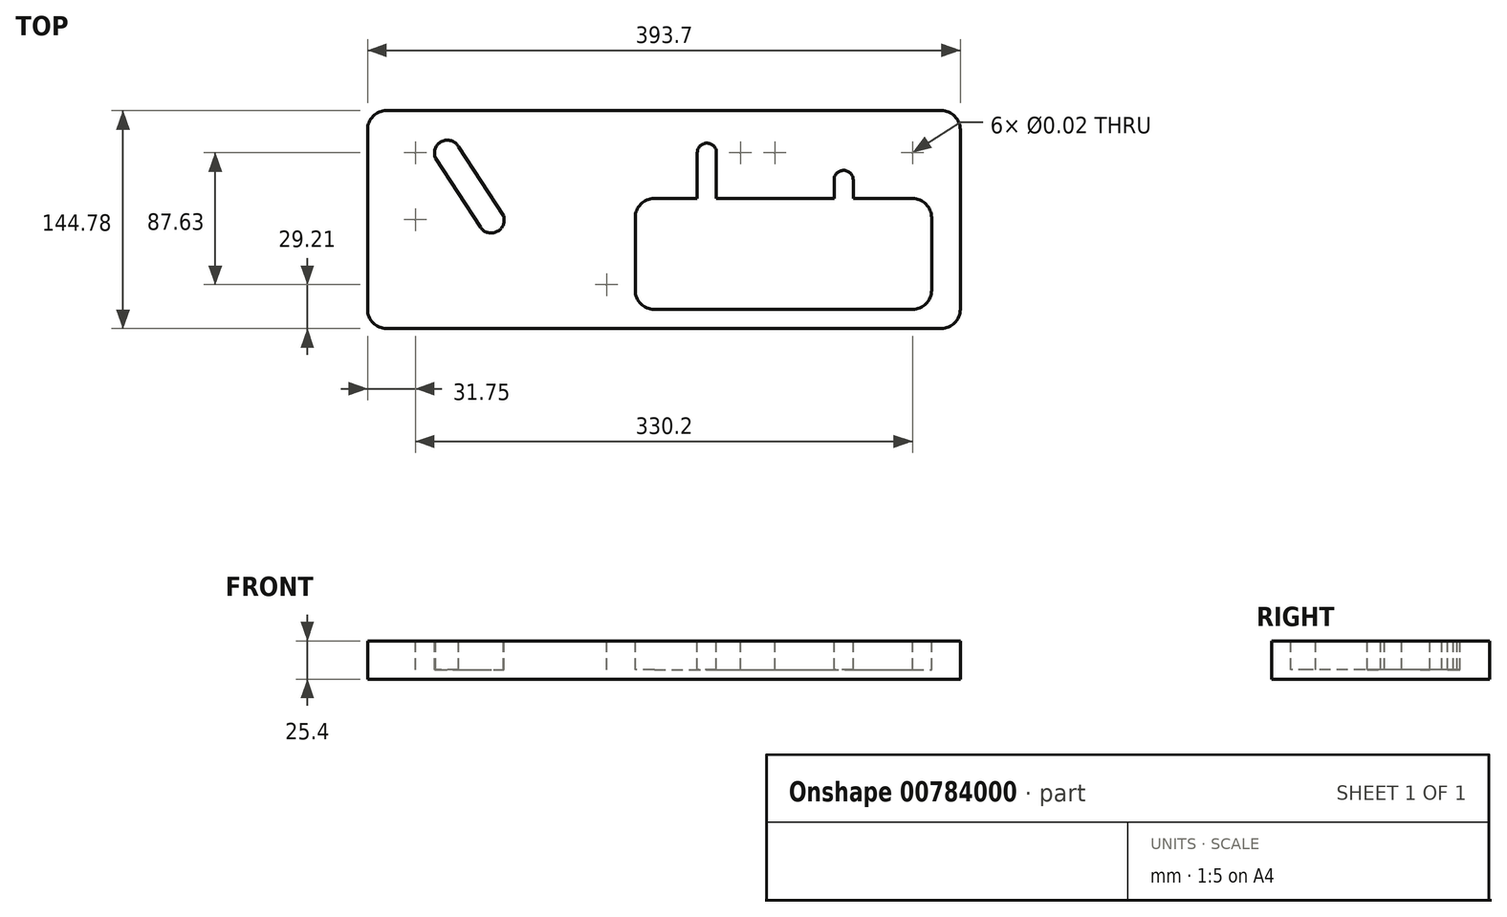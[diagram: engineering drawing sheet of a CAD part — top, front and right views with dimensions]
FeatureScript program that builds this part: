
annotation { "Feature Type Name" : "Feature", "Feature Type Description" : "" }
export const myFeature = defineFeature(function(context is Context, id is Id, definition is map)
    precondition{}
    {
        {
            var Q0;
            Q0=qCreatedBy(makeId("Top.planeOp"),FACE);
            var sketch = newSketch(context, id + "F0", { "sketchPlane" : qUnion([Q0])});
            skLineSegment(sketch, "E0.bottom", {"start": v(-184.15, -72.4) * mm, "end": v(184.15, -72.4) * mm});
            skLineSegment(sketch, "E0.top", {"start": v(-184.15, 72.4) * mm, "end": v(184.15, 72.4) * mm});
            skLineSegment(sketch, "E0.left", {"start": v(-196.85, -59.7) * mm, "end": v(-196.85, 59.7) * mm});
            skLineSegment(sketch, "E0.right", {"start": v(196.85, -59.7) * mm, "end": v(196.85, 59.7) * mm});
            skPoint(sketch, "E0.middle", {"position": v(0, 0) * mm});
            skPoint(sketch, "E1.visualSharp", {"position": v(-196.85, 72.4) * mm});
            skArc(sketch, "E1.filletArc", {"start": v(-184.15, 72.4) * mm, "mid": v(-193.13, 68.67) * mm, "end": v(-196.85, 59.7) * mm});
            skPoint(sketch, "E2.visualSharp", {"position": v(-196.85, -72.4) * mm});
            skArc(sketch, "E2.filletArc", {"start": v(-196.85, -59.7) * mm, "mid": v(-193.13, -68.67) * mm, "end": v(-184.15, -72.4) * mm});
            skPoint(sketch, "E3.visualSharp", {"position": v(196.85, 72.4) * mm});
            skArc(sketch, "E3.filletArc", {"start": v(196.85, 59.7) * mm, "mid": v(193.13, 68.67) * mm, "end": v(184.15, 72.4) * mm});
            skPoint(sketch, "E4.visualSharp", {"position": v(196.85, -72.4) * mm});
            skArc(sketch, "E4.filletArc", {"start": v(184.15, -72.4) * mm, "mid": v(193.13, -68.67) * mm, "end": v(196.85, -59.7) * mm});
            skSolve(sketch);
        }
        {
            var Q0;
            Q0 = qSketchRegion(id + "F0", true);
            extrude(context, id + "F1", {"entities" : qUnion([Q0]), "depth" : -25.4 * mm, "offsetDistance" : 25.4 * mm});
        }
        {
            var Q0;
            Q0=qCreatedBy(makeId("Top.planeOp"),FACE);
            var sketch = newSketch(context, id + "F2", { "sketchPlane" : qUnion([Q0])});
            skLineSegment(sketch, "E5.bottom", {"start": v(-6.35, 13.97) * mm, "end": v(165.1, 13.97) * mm});
            skLineSegment(sketch, "E5.top", {"start": v(-6.35, -59.7) * mm, "end": v(165.1, -59.7) * mm});
            skLineSegment(sketch, "E5.left", {"start": v(-19.05, 1.27) * mm, "end": v(-19.05, -47) * mm});
            skLineSegment(sketch, "E5.right", {"start": v(177.8, 1.27) * mm, "end": v(177.8, -47) * mm});
            skPoint(sketch, "E6.visualSharp", {"position": v(-19.05, 13.97) * mm});
            skArc(sketch, "E6.filletArc", {"start": v(-6.35, 13.97) * mm, "mid": v(-15.33, 10.25) * mm, "end": v(-19.05, 1.27) * mm});
            skPoint(sketch, "E7.visualSharp", {"position": v(177.8, 13.97) * mm});
            skArc(sketch, "E7.filletArc", {"start": v(177.8, 1.27) * mm, "mid": v(174.08, 10.25) * mm, "end": v(165.1, 13.97) * mm});
            skPoint(sketch, "E8.visualSharp", {"position": v(177.8, -59.7) * mm});
            skArc(sketch, "E8.filletArc", {"start": v(165.1, -59.7) * mm, "mid": v(174.08, -55.97) * mm, "end": v(177.8, -47) * mm});
            skPoint(sketch, "E9.visualSharp", {"position": v(-19.05, -59.7) * mm});
            skArc(sketch, "E9.filletArc", {"start": v(-19.05, -47) * mm, "mid": v(-15.33, -55.97) * mm, "end": v(-6.35, -59.7) * mm});
            skPoint(sketch, "E10", {"position": v(-165.1, 44.45) * mm});
            skPoint(sketch, "E11", {"position": v(28.78, 44.45) * mm});
            skPoint(sketch, "E12", {"position": v(50.8, 44.45) * mm});
            skPoint(sketch, "E13", {"position": v(73.66, 44.45) * mm});
            skPoint(sketch, "E14", {"position": v(165.1, 44.45) * mm});
            skPoint(sketch, "E15", {"position": v(-165.1, 0) * mm});
            skPoint(sketch, "E16", {"position": v(-114.3, 0) * mm});
            skLineSegment(sketch, "E17", {"start": v(-151.6, 40.57) * mm, "end": v(-121.93, -5.03) * mm});
            skLineSegment(sketch, "E18", {"start": v(-136.26, 48.24) * mm, "end": v(-106.6, 2.64) * mm});
            skLineSegment(sketch, "E19.top", {"start": v(22.2, 13.97) * mm, "end": v(34.9, 13.97) * mm});
            skLineSegment(sketch, "E19.left", {"start": v(22.2, 44.45) * mm, "end": v(22.2, 13.97) * mm});
            skLineSegment(sketch, "E19.right", {"start": v(34.9, 44.45) * mm, "end": v(34.9, 13.97) * mm});
            skArc(sketch, "E20", {"start": v(34.9, 44.45) * mm, "mid": v(28.54, 50.8) * mm, "end": v(22.2, 44.45) * mm});
            skLineSegment(sketch, "E21.top", {"start": v(113.03, 13.97) * mm, "end": v(125.73, 13.97) * mm});
            skLineSegment(sketch, "E21.left", {"start": v(113.03, 26.33) * mm, "end": v(113.03, 13.97) * mm});
            skLineSegment(sketch, "E21.right", {"start": v(125.73, 26.33) * mm, "end": v(125.73, 13.97) * mm});
            skArc(sketch, "E22", {"start": v(125.73, 26.33) * mm, "mid": v(119.38, 32.68) * mm, "end": v(113.03, 26.33) * mm});
            skPoint(sketch, "E23", {"position": v(-38.1, -43.18) * mm});
            skArc(sketch, "E24", {"start": v(-136.26, 48.24) * mm, "mid": v(-147.64, 51.83) * mm, "end": v(-151.6, 40.57) * mm});
            skArc(sketch, "E25", {"start": v(-121.93, -5.03) * mm, "mid": v(-110.84, -8.04) * mm, "end": v(-106.6, 2.64) * mm});
            skSolve(sketch);
        }
        {
            var Q0;
            Q0 = qSketchRegion(id + "F2", true);
            extrude(context, id + "F3", {"entities" : qUnion([Q0]), "operationType" : NewBodyOperationType.REMOVE, "oppositeDirection" : true, "depth" : 19.05 * mm, "offsetDistance" : 25.4 * mm});
        }
        {
            var Q0;
            Q0=sQuery(id+"F2.wireOp",VERTEX,"E10");
            var Q1;
            Q1=sQuery(id+"F2.wireOp",VERTEX,"E12");
            var Q2;
            Q2=sQuery(id+"F2.wireOp",VERTEX,"E13");
            var Q3;
            Q3=sQuery(id+"F2.wireOp",VERTEX,"E14");
            var Q4;
            Q4=sQuery(id+"F2.wireOp",VERTEX,"E15");
            var Q5;
            Q5=sQuery(id+"F2.wireOp",VERTEX,"E23");
            var Q6;
            Q6=makeQuery(id+"F1.opExtrude","SWEPT_BODY",BODY,{"disambiguationData":[OSD([sQuery(id+"F0.wireOp",EDGE,"E0.bottom"),sQuery(id+"F0.wireOp",EDGE,"E0.top"),sQuery(id+"F0.wireOp",EDGE,"E0.left"),sQuery(id+"F0.wireOp",EDGE,"E0.right"),sQuery(id+"F0.wireOp",EDGE,"E1.filletArc"),sQuery(id+"F0.wireOp",EDGE,"E2.filletArc"),sQuery(id+"F0.wireOp",EDGE,"E3.filletArc"),sQuery(id+"F0.wireOp",EDGE,"E4.filletArc")])]});
            hole(context, id + "F4", {"style" : HoleStyle.SIMPLE, "endStyle" : HoleEndStyle.BLIND, "standardTappedOrClearance" : lookupTablePath({ "standard" : "ANSI", "size" : "5/8 (0.62)", "type" : "Drilled" }), "standardBlindInLast" : lookupTablePath({ "standard" : "ANSI", "size" : "5/8 (0.62)", "type" : "Drilled" }), "holeDiameter" : 5 / 203.2 * mm, "majorDiameter" : 4.17 * mm, "holeDepth" : 19.05 * mm, "tappedDepth" : 16.67 * mm, "tapClearance" : 3, "locations" : qUnion([Q0, Q1, Q2, Q3, Q4, Q5]), "scope" : qUnion([Q6])});
        }
    });
